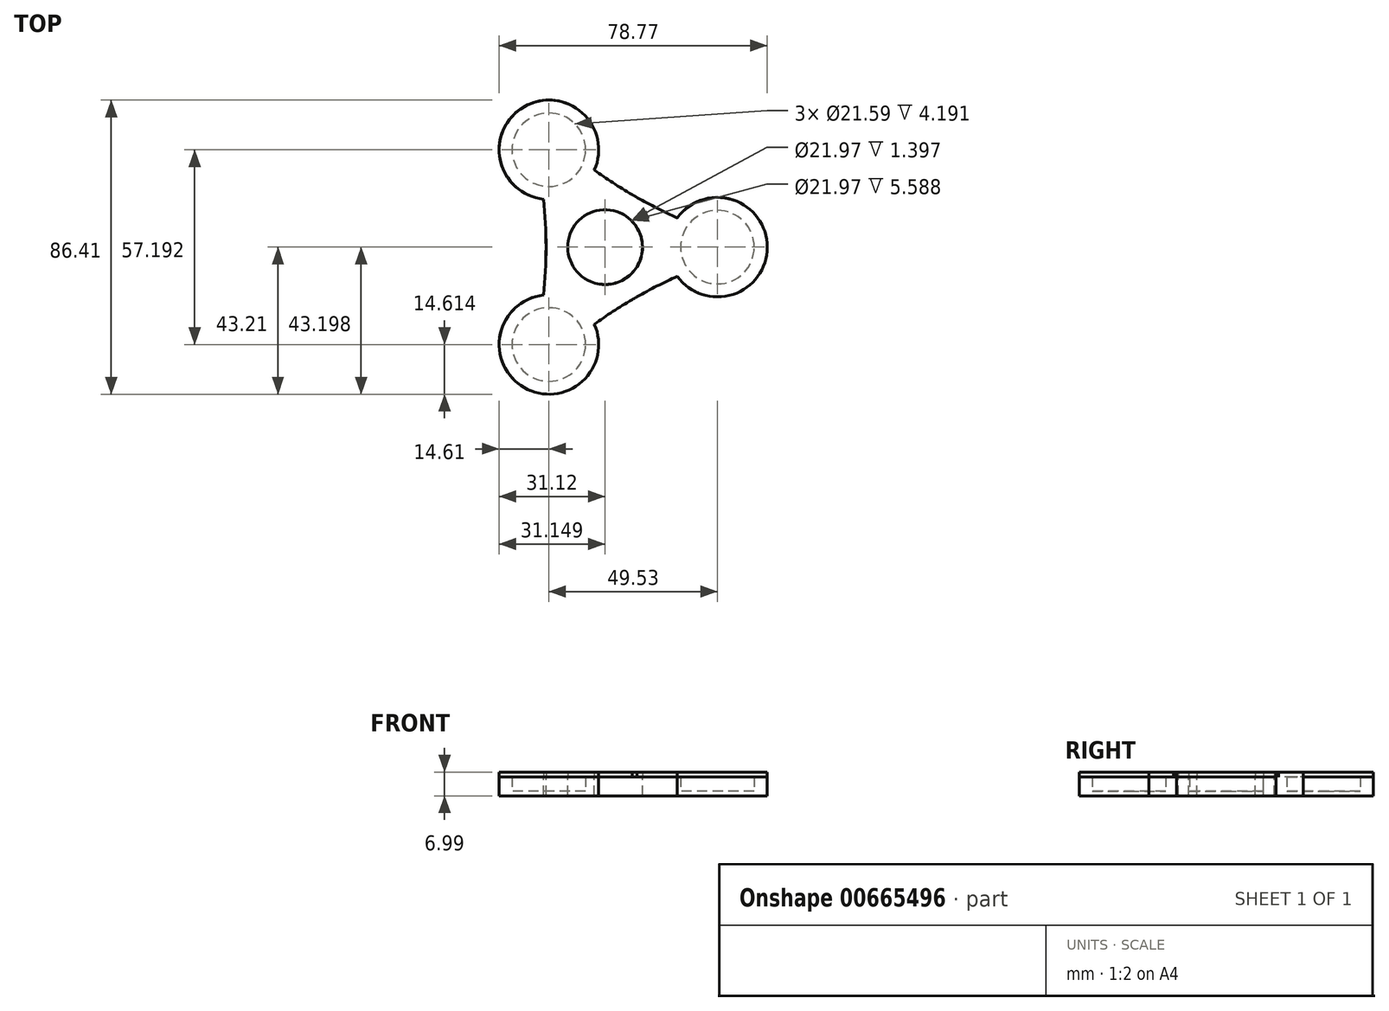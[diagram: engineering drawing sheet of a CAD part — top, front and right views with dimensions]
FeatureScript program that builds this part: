
annotation { "Feature Type Name" : "Feature", "Feature Type Description" : "" }
export const myFeature = defineFeature(function(context is Context, id is Id, definition is map)
    precondition{}
    {
        {
            var Q0;
            Q0=qCreatedBy(makeId("Top.planeOp"),FACE);
            var sketch = newSketch(context, id + "F0", { "sketchPlane" : qUnion([Q0])});
            skCircle(sketch, "E0", {"center": v(0, 0) * mm, "radius": 10.99 * mm});
            skCircle(sketch, "E1", {"center": v(33.02, 0) * mm, "radius": 10.8 * mm});
            skCircle(sketch, "E2.1.0", {"center": v(-16.5, 28.6) * mm, "radius": 10.8 * mm});
            skCircle(sketch, "E2.2.0", {"center": v(-16.51, -28.6) * mm, "radius": 10.8 * mm});
            skArc(sketch, "E3.0", {"start": v(-3.16, 22.67) * mm, "mid": v(-23.8, 41.25) * mm, "end": v(-18.08, 14.08) * mm});
            skArc(sketch, "E4.0", {"start": v(21.21, -8.6) * mm, "mid": v(47.62, 0) * mm, "end": v(21.21, 8.6) * mm});
            skArc(sketch, "E5.0", {"start": v(-18.08, -14.08) * mm, "mid": v(-23.8, -41.25) * mm, "end": v(-3.16, -22.67) * mm});
            skArc(sketch, "E6.0", {"start": v(7.92, -15.42) * mm, "mid": v(8.67, -15.01) * mm, "end": v(9.4, -14.57) * mm});
            skArc(sketch, "E7.trimOffspring", {"start": v(-3.16, 22.67) * mm, "mid": v(8.66, 15) * mm, "end": v(21.21, 8.6) * mm});
            skArc(sketch, "E8.trimOffspring", {"start": v(21.21, -8.6) * mm, "mid": v(8.66, -15) * mm, "end": v(-3.16, -22.67) * mm});
            skArc(sketch, "E9.trimOffspring", {"start": v(9.41, 14.56) * mm, "mid": v(8.67, 15.01) * mm, "end": v(7.9, 15.43) * mm});
            skArc(sketch, "E10.trimOffspring", {"start": v(-18.08, -14.08) * mm, "mid": v(-17.34, 0) * mm, "end": v(-18.08, 14.08) * mm});
            skSolve(sketch);
        }
        {
            var Q0;
            Q0=makeQuery(id+"F0.imprint","IMPRINT",FACE,{"disambiguationData":[TD([[makeQuery(id+"F0.imprint","IMPRINT",EDGE,{"derivedFrom":sQuery(id+"F0.wireOp",EDGE,"E2.1.0")}),1.0]])]});
            var Q1;
            Q1=makeQuery(id+"F0.imprint","IMPRINT",FACE,{"disambiguationData":[TD([[makeQuery(id+"F0.imprint","IMPRINT",EDGE,{"derivedFrom":sQuery(id+"F0.wireOp",EDGE,"E0")}),-1.0]])]});
            var Q2;
            Q2=makeQuery(id+"F0.imprint","IMPRINT",FACE,{"disambiguationData":[TD([[makeQuery(id+"F0.imprint","IMPRINT",EDGE,{"derivedFrom":sQuery(id+"F0.wireOp",EDGE,"E1")}),1.0]])]});
            var Q3;
            Q3=makeQuery(id+"F0.imprint","IMPRINT",FACE,{"disambiguationData":[TD([[makeQuery(id+"F0.imprint","IMPRINT",EDGE,{"derivedFrom":sQuery(id+"F0.wireOp",EDGE,"E2.2.0")}),1.0]])]});
            extrude(context, id + "F1", {"entities" : qUnion([Q0, Q1, Q2, Q3]), "oppositeDirection" : true, "depth" : 1.4 * mm, "offsetDistance" : 25.4 * mm});
        }
        {
            var Q0;
            Q0=makeQuery(id+"F0.imprint","IMPRINT",FACE,{"disambiguationData":[TD([[makeQuery(id+"F0.imprint","IMPRINT",EDGE,{"derivedFrom":sQuery(id+"F0.wireOp",EDGE,"E0")}),-1.0]])]});
            extrude(context, id + "F2", {"entities" : qUnion([Q0]), "operationType" : NewBodyOperationType.ADD, "depth" : 4.2 * mm, "offsetDistance" : 25.4 * mm});
        }
        {
            var Q0;
            Q0=makeQuery(id+"F2.opExtrude","CAP_FACE",FACE,{"disambiguationData":[OSD([sQuery(id+"F0.wireOp",EDGE,"E0"),sQuery(id+"F0.wireOp",EDGE,"E1"),sQuery(id+"F0.wireOp",EDGE,"E2.1.0"),sQuery(id+"F0.wireOp",EDGE,"E2.2.0"),sQuery(id+"F0.wireOp",EDGE,"E3.0"),sQuery(id+"F0.wireOp",EDGE,"E4.0"),sQuery(id+"F0.wireOp",EDGE,"E5.0"),sQuery(id+"F0.wireOp",EDGE,"E7.trimOffspring"),sQuery(id+"F0.wireOp",EDGE,"E8.trimOffspring"),sQuery(id+"F0.wireOp",EDGE,"E10.trimOffspring")])],"isStart":false});
            cPlane(context, id + "F3", {"entities" : qUnion([Q0]), "cplaneType" : CPlaneType.OFFSET, "offset" : 0 * mm, "width" : 152.4 * mm, "height" : 152.4 * mm});
        }
        {
            var Q0;
            Q0=qCreatedBy(id+"F3.planeOp",FACE);
            var sketch = newSketch(context, id + "F4", { "sketchPlane" : qUnion([Q0])});
            skCircle(sketch, "E11", {"center": v(0.03, -0.01) * mm, "radius": 10.99 * mm});
            skCircle(sketch, "E12", {"center": v(33.05, -0.01) * mm, "radius": 10.8 * mm});
            skCircle(sketch, "E13.1.0", {"center": v(-16.48, 28.58) * mm, "radius": 10.8 * mm});
            skCircle(sketch, "E13.2.0", {"center": v(-16.48, -28.6) * mm, "radius": 10.8 * mm});
            skArc(sketch, "E14.0", {"start": v(-3.13, 22.66) * mm, "mid": v(-23.77, 41.24) * mm, "end": v(-18.05, 14.06) * mm});
            skArc(sketch, "E15.0", {"start": v(21.24, -8.6) * mm, "mid": v(47.65, -0.01) * mm, "end": v(21.24, 8.58) * mm});
            skArc(sketch, "E16.0", {"start": v(-18.05, -14.09) * mm, "mid": v(-23.77, -41.26) * mm, "end": v(-3.13, -22.68) * mm});
            skArc(sketch, "E17.0", {"start": v(7.95, -15.43) * mm, "mid": v(8.7, -15.03) * mm, "end": v(9.43, -14.58) * mm});
            skArc(sketch, "E18.trimOffspring", {"start": v(-3.13, 22.66) * mm, "mid": v(8.68, 14.98) * mm, "end": v(21.24, 8.58) * mm});
            skArc(sketch, "E19.trimOffspring", {"start": v(21.24, -8.6) * mm, "mid": v(8.68, -15) * mm, "end": v(-3.13, -22.68) * mm});
            skArc(sketch, "E20.trimOffspring", {"start": v(9.44, 14.55) * mm, "mid": v(8.7, 15) * mm, "end": v(7.93, 15.42) * mm});
            skArc(sketch, "E21.trimOffspring", {"start": v(-18.05, -14.09) * mm, "mid": v(-17.31, -0.01) * mm, "end": v(-18.05, 14.06) * mm});
            skSolve(sketch);
        }
        {
            var Q0;
            {var subQ0=sQuery(id+"F4.wireOp",EDGE,"E17.0");Q0=makeQuery(id+"F4.imprint","IMPRINT",FACE,{"disambiguationData":[TD([[makeQuery(id+"F4.imprint","IMPRINT",EDGE,{"derivedFrom":subQ0}),1.0]])]});}
            var Q1;
            {var subQ0=sQuery(id+"F4.wireOp",EDGE,"E20.trimOffspring");Q1=makeQuery(id+"F4.imprint","IMPRINT",FACE,{"disambiguationData":[TD([[makeQuery(id+"F4.imprint","IMPRINT",EDGE,{"derivedFrom":subQ0}),1.0]])]});}
            var Q2;
            Q2=makeQuery(id+"F4.imprint","IMPRINT",FACE,{"disambiguationData":[TD([[makeQuery(id+"F4.imprint","IMPRINT",EDGE,{"derivedFrom":sQuery(id+"F4.wireOp",EDGE,"E13.2.0")}),1.0]])]});
            var Q3;
            Q3=makeQuery(id+"F4.imprint","IMPRINT",FACE,{"disambiguationData":[TD([[makeQuery(id+"F4.imprint","IMPRINT",EDGE,{"derivedFrom":sQuery(id+"F4.wireOp",EDGE,"E13.1.0")}),1.0]])]});
            var Q4;
            Q4=makeQuery(id+"F4.imprint","IMPRINT",FACE,{"disambiguationData":[TD([[makeQuery(id+"F4.imprint","IMPRINT",EDGE,{"derivedFrom":sQuery(id+"F4.wireOp",EDGE,"E12")}),1.0]])]});
            var Q5;
            Q5=makeQuery(id+"F4.imprint","IMPRINT",FACE,{"disambiguationData":[TD([[makeQuery(id+"F4.imprint","IMPRINT",EDGE,{"derivedFrom":sQuery(id+"F4.wireOp",EDGE,"E11")}),-1.0]])]});
            extrude(context, id + "F5", {"entities" : qUnion([Q0, Q1, Q2, Q3, Q4, Q5]), "operationType" : NewBodyOperationType.ADD, "depth" : 1.4 * mm, "offsetDistance" : 25.4 * mm});
        }
    });
